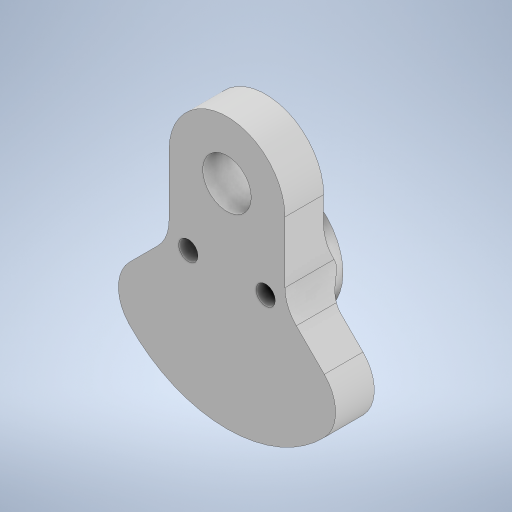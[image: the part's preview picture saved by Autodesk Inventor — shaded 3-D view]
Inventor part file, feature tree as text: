
AUTODESK INVENTOR PART (.ipt)
format: ipt  version: 2023 (Build 270158000, 158)  size: 655,360 bytes
history: native  units: in
note: dims shown in document units (in); Inventor stores cm internally (conversion verified against a paired STEP export)
features: extrude x2, sketch x1, fillet x1
ambient origin geometry x8: Origin, YZ Plane, XZ Plane, XY Plane, X Axis, Y Axis, Z Axis, Center Point
bodies: Body1 (feature_tree)
feature tree (4):
  sketch  "Sketch1"  dims[d3=0.866in d15=0.75in d20=0.314in d31=0.25in d32=0.0in d34=1.75in d35=0.25in d36=0.25in d37=0.75in d38=0.5in d39=0.125in d40=0.0in d41=0.125in]
  extrude  "Extrusion2"  Depth=0.125in
  extrude  "Extrusion3"  Depth=0.25in TaperAngle=0.0deg
  fillet  "Fillet1"  Radius=1.75in
